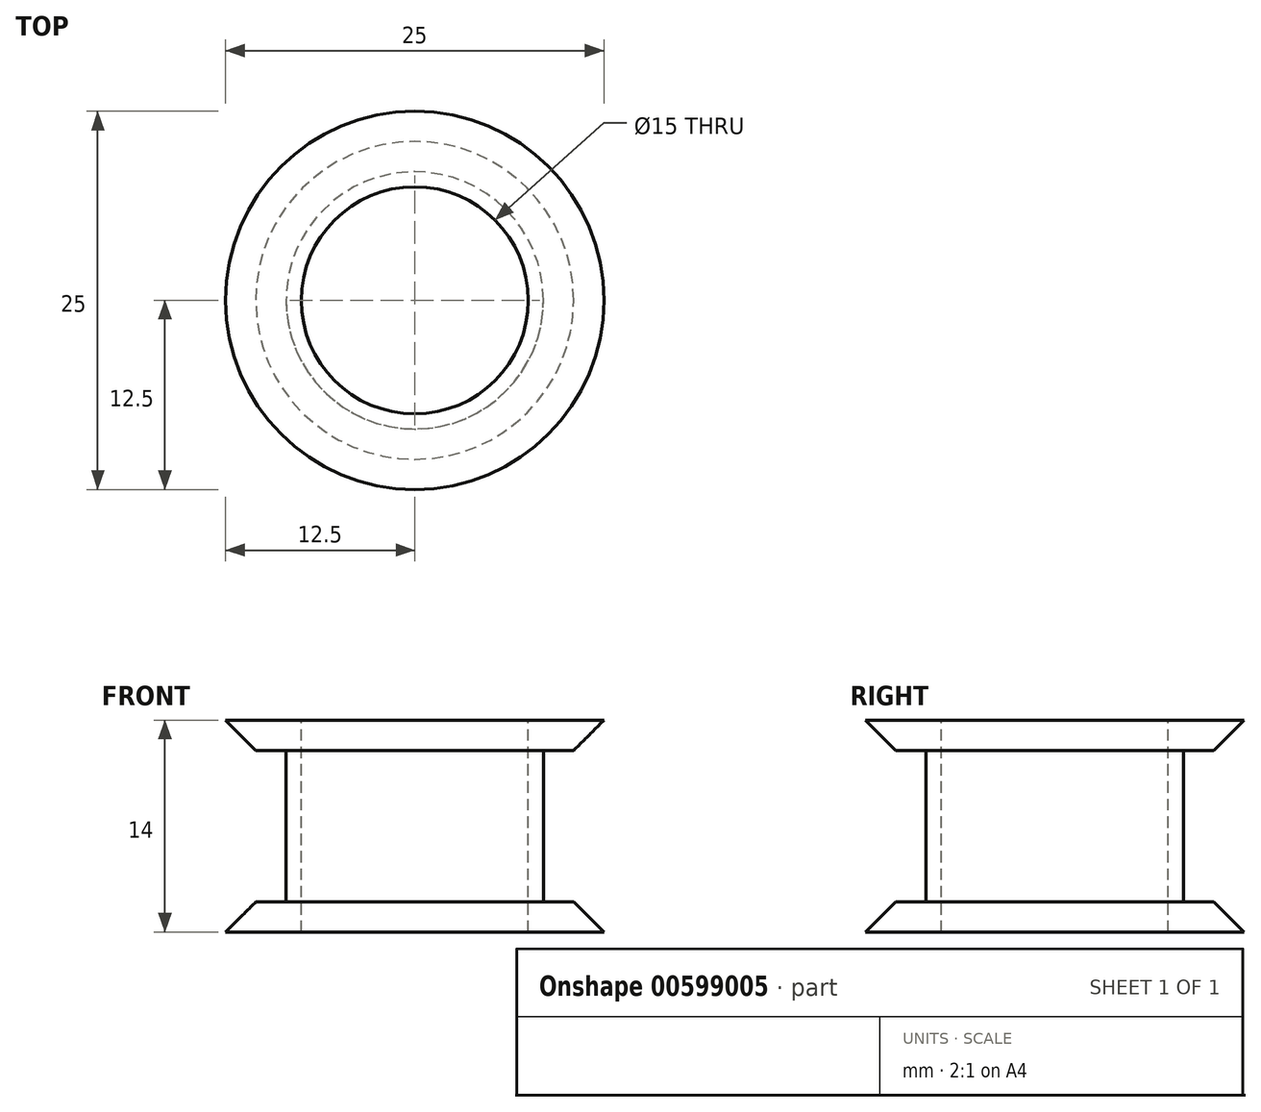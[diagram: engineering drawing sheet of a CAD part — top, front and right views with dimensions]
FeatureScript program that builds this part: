
annotation { "Feature Type Name" : "Feature", "Feature Type Description" : "" }
export const myFeature = defineFeature(function(context is Context, id is Id, definition is map)
    precondition{}
    {
        {
            var Q0;
            Q0=qCreatedBy(makeId("Top.planeOp"),FACE);
            var sketch = newSketch(context, id + "F0", { "sketchPlane" : qUnion([Q0])});
            skCircle(sketch, "E0", {"center": v(0, 0) * mm, "radius": 8.5 * mm});
            skSolve(sketch);
        }
        {
            var Q0;
            Q0 = qSketchRegion(id + "F0", true);
            extrude(context, id + "F1", {"entities" : qUnion([Q0]), "depth" : 14 * mm, "offsetDistance" : 25 * mm});
        }
        {
            var Q0;
            Q0=makeQuery(id+"F1.opExtrude","CAP_FACE",FACE,{"disambiguationData":[OSD([sQuery(id+"F0.wireOp",EDGE,"E0")])],"isStart":false});
            var sketch = newSketch(context, id + "F2", { "sketchPlane" : qUnion([Q0])});
            skCircle(sketch, "E1", {"center": v(0, 0) * mm, "radius": 12.5 * mm});
            skSolve(sketch);
        }
        {
            var Q0;
            Q0=makeQuery(id+"F1.opExtrude","CAP_FACE",FACE,{"disambiguationData":[OSD([sQuery(id+"F0.wireOp",EDGE,"E0")])],"isStart":true});
            var sketch = newSketch(context, id + "F3", { "sketchPlane" : qUnion([Q0])});
            skCircle(sketch, "E2", {"center": v(0, 0) * mm, "radius": 12.5 * mm});
            skSolve(sketch);
        }
        {
            var Q0;
            Q0=makeQuery(id+"F2.imprint","IMPRINT",FACE,{"disambiguationData":[TD([[makeQuery(id+"F2.imprint","IMPRINT",EDGE,{"derivedFrom":sQuery(id+"F2.wireOp",EDGE,"E1")}),1.0]])]});
            extrude(context, id + "F4", {"entities" : qUnion([Q0]), "operationType" : NewBodyOperationType.ADD, "oppositeDirection" : true, "depth" : 2 * mm, "offsetDistance" : 25 * mm});
        }
        {
            var Q0;
            Q0=makeQuery(id+"F4.opExtrude","CAP_EDGE",EDGE,{"disambiguationData":[OSD([sQuery(id+"F2.wireOp",EDGE,"E1")])],"isStart":false});
            chamfer(context, id + "F5", {"entities" : qUnion([Q0]), "width" : 2 * mm, "tangentPropagation" : true});
        }
        {
            var Q0;
            Q0=makeQuery(id+"F3.imprint","IMPRINT",FACE,{"disambiguationData":[TD([[makeQuery(id+"F3.imprint","IMPRINT",EDGE,{"derivedFrom":sQuery(id+"F3.wireOp",EDGE,"E2")}),1.0]])]});
            extrude(context, id + "F6", {"entities" : qUnion([Q0]), "operationType" : NewBodyOperationType.ADD, "oppositeDirection" : true, "depth" : 2 * mm, "offsetDistance" : 25 * mm});
        }
        {
            var Q0;
            Q0=makeQuery(id+"F6.opExtrude","CAP_EDGE",EDGE,{"disambiguationData":[OSD([sQuery(id+"F3.wireOp",EDGE,"E2")])],"isStart":false});
            chamfer(context, id + "F7", {"entities" : qUnion([Q0]), "width" : 2 * mm, "tangentPropagation" : true});
        }
        {
            var Q0;
            {var subQ0=sQuery(id+"F0.wireOp",EDGE,"E0");Q0=makeQuery(id+"F4.boolean.opBoolean","MERGE",FACE,{"derivedFrom":[makeQuery(id+"F1.opExtrude","CAP_FACE",FACE,{"disambiguationData":[OSD([subQ0])],"isStart":false}),makeQuery(id+"F4.opExtrude","CAP_FACE",FACE,{"disambiguationData":[OSD([subQ0,sQuery(id+"F2.wireOp",EDGE,"E1")])],"isStart":true})]});}
            var sketch = newSketch(context, id + "F8", { "sketchPlane" : qUnion([Q0])});
            skCircle(sketch, "E3", {"center": v(0, 0) * mm, "radius": 7.5 * mm});
            skSolve(sketch);
        }
        {
            var Q0;
            Q0 = qSketchRegion(id + "F8", true);
            extrude(context, id + "F9", {"entities" : qUnion([Q0]), "operationType" : NewBodyOperationType.REMOVE, "endBound" : BoundingType.THROUGH_ALL, "oppositeDirection" : true, "depth" : 25 * mm, "offsetDistance" : 25 * mm});
        }
    });
